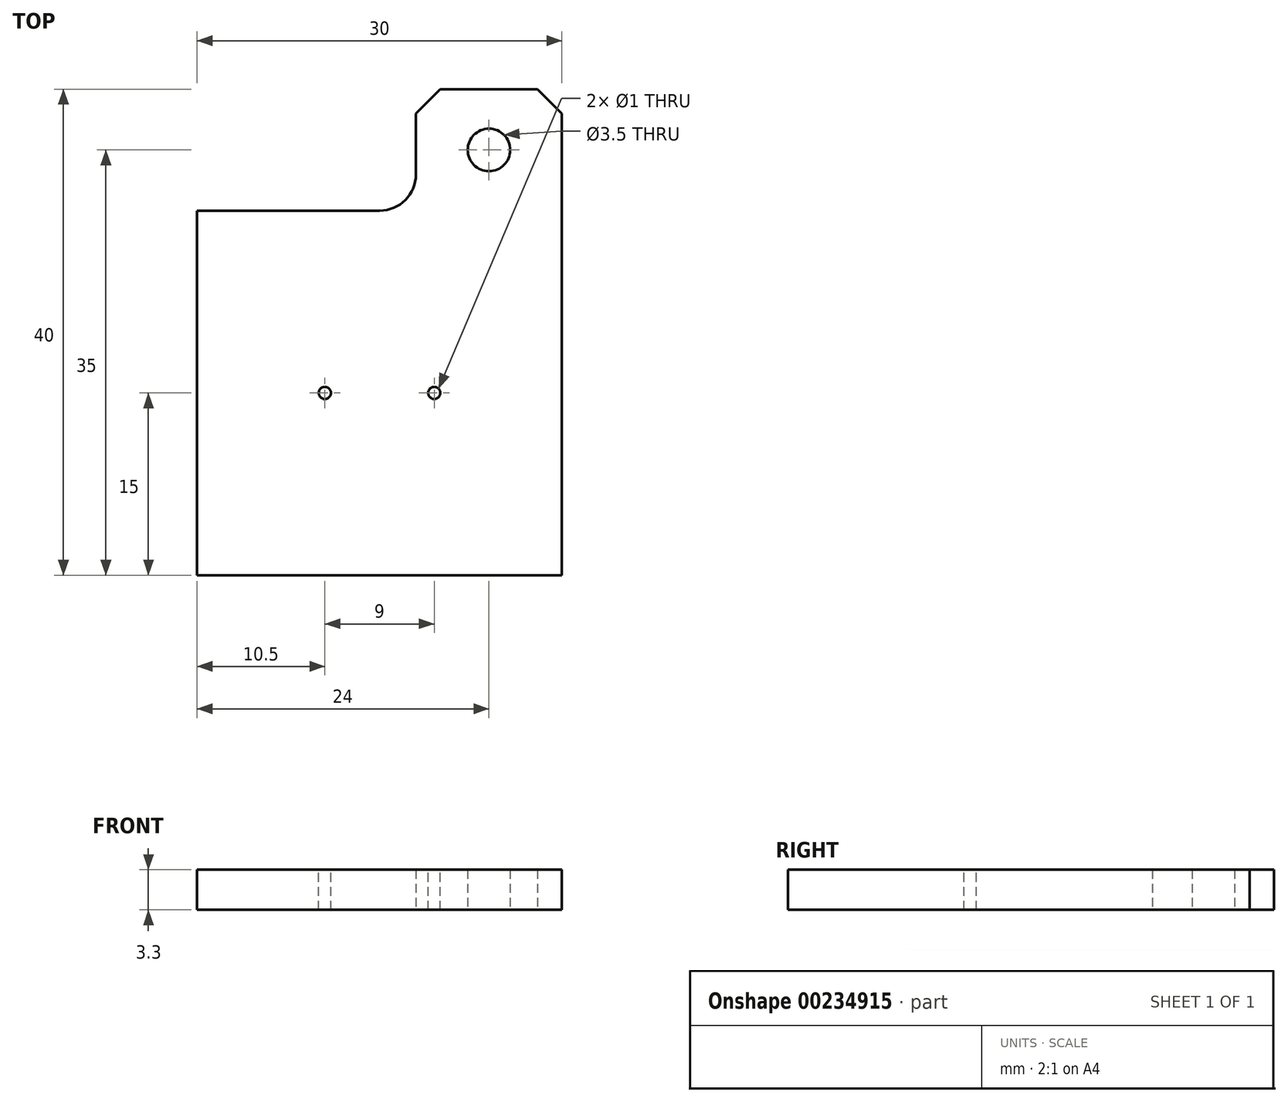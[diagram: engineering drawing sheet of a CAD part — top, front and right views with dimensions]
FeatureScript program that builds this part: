
annotation { "Feature Type Name" : "Feature", "Feature Type Description" : "" }
export const myFeature = defineFeature(function(context is Context, id is Id, definition is map)
    precondition{}
    {
        {
            var Q0;
            Q0=qCreatedBy(makeId("Top.planeOp"),FACE);
            var sketch = newSketch(context, id + "F0", { "sketchPlane" : qUnion([Q0])});
            skLineSegment(sketch, "E0.bottom", {"start": v(15, 15) * mm, "end": v(-15, 15) * mm});
            skLineSegment(sketch, "E0.top", {"start": v(15, -15) * mm, "end": v(-15, -15) * mm});
            skLineSegment(sketch, "E0.left", {"start": v(15, 15) * mm, "end": v(15, -15) * mm});
            skLineSegment(sketch, "E0.right", {"start": v(-15, 15) * mm, "end": v(-15, -15) * mm});
            skPoint(sketch, "E0.middle", {"position": v(0, 0) * mm});
            skLineSegment(sketch, "E1.bottom", {"start": v(15, 15) * mm, "end": v(3, 15) * mm});
            skLineSegment(sketch, "E1.top", {"start": v(15, 25) * mm, "end": v(3, 25) * mm});
            skLineSegment(sketch, "E1.left", {"start": v(15, 15) * mm, "end": v(15, 25) * mm});
            skLineSegment(sketch, "E1.right", {"start": v(3, 15) * mm, "end": v(3, 25) * mm});
            skLineSegment(sketch, "E2", {"start": v(9, 25) * mm, "end": v(9, 15) * mm, "construction": true});
            skLineSegment(sketch, "E3", {"start": v(3, 20) * mm, "end": v(15, 20) * mm, "construction": true});
            skCircle(sketch, "E4", {"center": v(9, 20) * mm, "radius": 1.75 * mm});
            skSolve(sketch);
        }
        {
            var Q0;
            Q0 = qSketchRegion(id + "F0", true);
            extrude(context, id + "F1", {"entities" : qUnion([Q0]), "depth" : 3.3 * mm});
        }
        {
            var Q0;
            Q0=makeQuery(id+"F1.opExtrude","SWEPT_EDGE",EDGE,{"disambiguationData":[OSD([sQuery(id+"F0.wireOp",EDGE,"E1.top"),sQuery(id+"F0.wireOp",EDGE,"E1.right")])]});
            var Q1;
            Q1=makeQuery(id+"F1.opExtrude","SWEPT_EDGE",EDGE,{"disambiguationData":[OSD([sQuery(id+"F0.wireOp",EDGE,"E1.top"),sQuery(id+"F0.wireOp",EDGE,"E1.left")])]});
            chamfer(context, id + "F2", {"entities" : qUnion([Q0, Q1]), "width" : 2 * mm, "tangentPropagation" : true});
        }
        {
            var Q0;
            Q0=makeQuery(id+"F1.opExtrude","SWEPT_EDGE",EDGE,{"disambiguationData":[OSD([sQuery(id+"F0.wireOp",EDGE,"E0.bottom"),sQuery(id+"F0.wireOp",EDGE,"E1.bottom"),sQuery(id+"F0.wireOp",EDGE,"E1.right")])]});
            fillet(context, id + "F3", {"entities" : qUnion([Q0]), "radius" : 3 * mm, "tangentPropagation" : true, "allowEdgeOverflow" : false});
        }
        {
            var Q0;
            Q0=makeQuery(id+"F1.opExtrude","CAP_FACE",FACE,{"disambiguationData":[OSD([sQuery(id+"F0.wireOp",EDGE,"E0.bottom"),sQuery(id+"F0.wireOp",EDGE,"E0.top"),sQuery(id+"F0.wireOp",EDGE,"E0.left"),sQuery(id+"F0.wireOp",EDGE,"E0.right"),sQuery(id+"F0.wireOp",EDGE,"E1.top"),sQuery(id+"F0.wireOp",EDGE,"E1.left"),sQuery(id+"F0.wireOp",EDGE,"E1.right"),sQuery(id+"F0.wireOp",EDGE,"E4")])],"isStart":false});
            var sketch = newSketch(context, id + "F4", { "sketchPlane" : qUnion([Q0])});
            skCircle(sketch, "E5", {"center": v(0, 0) * mm, "radius": 5 * mm, "construction": true});
            skCircle(sketch, "E6", {"center": v(0, 0) * mm, "radius": 4.5 * mm, "construction": true});
            skLineSegment(sketch, "E7", {"start": v(-5, 0) * mm, "end": v(5, 0) * mm, "construction": true});
            skCircle(sketch, "E8", {"center": v(-4.5, 0) * mm, "radius": 0.5 * mm});
            skCircle(sketch, "E9", {"center": v(4.5, 0) * mm, "radius": 0.5 * mm});
            skSolve(sketch);
        }
        {
            var Q0;
            Q0 = qSketchRegion(id + "F4", true);
            extrude(context, id + "F5", {"entities" : qUnion([Q0]), "operationType" : NewBodyOperationType.REMOVE, "oppositeDirection" : true, "depth" : 25 * mm});
        }
    });
